# Revit family: Haworth_Enclose-Wall-Solid_Transom1
name_source: partatom
category: Furniture Systems
units: mm (PartAtom-declared; Revit-internal decimal feet)

## family parameters
Always vertical = Yes
Cut with Voids When Loaded = No
OmniClass Number = 23.25.40.14
OmniClass Title = Demountable Partitions
Part Type = Normal
Room Calculation Point = No
Round Connector Dimension = Use Diameter
Shared = Yes
Work Plane-Based = No

## types (3) — shared parameters
# of Panels Back = 1
# of Panels Front = 1
Actual # of Panels Back = 1
Actual # of Panels Front = 1
Actual Panel 1 Back Height = 32 "
Actual Panel 1 Front Height = 32 "
Actual Panel 2 Back Height = 64 "
Actual Panel 2 Front Height = 64 "
Assembly Code = C1010200
Base Height = 1.25 "
Cap Height = 1 "
Ceiling Mount = Yes
Description = Enclose Solid Wall w/ Glass Transom
End of Run Finish = Haworth - Plastic - Black
End of Run Width = 0.155 "
Frame Depth = 4 "
Frame Finish = Haworth - Brushed Aluminum
Glass Finish = Haworth - Glass - Clear
Glass Offset = 4.745 "
Glass Panel Depth = 0.4 "
Horizontal Bottom Adjuster Width = 3.87 "
Horizontal Bottom Trim Width = 2.425 "
Horizontal Frame Width = 0.875 "
Horizontal Top Adjuster Width = 2.625 "
Horizontal Top Trim Width = 1.43 "
Horizontal Transom Frame Width = 1.625 "
LEED Data = www.haworth.com/_layouts/Haworth.ProductCatalog/Handlers/GetAsset.ashx/Enclose_LEED_Contribution.pdf?cid=180&rid=1981&type=Leed
Manufacturer = Haworth
Material Options = http://surfaces.haworth.com
Max # of Panels = 3
Max. Height = 144 "
Max. Width = 60 "
Min. Height = 92 "
Min. Width = 8 "
Min/Max Height = 92-144 in.
Min/Max Width = 8-60 in.
Model = see catalog for model #
Offset Back = 1.25 "
Offset Front = 1.25 "
Panel 1 Back Height = 32 "
Panel 1 Front Height = 32 "
Panel 2 Back Height = 64 "
Panel 2 Front Height = 64 "
Panel Depth = 0.5 "
Panel Height Note = All Heights are A.F.F.
Panel Size Note = 8in increments
Raceway Panel Back = No
Raceway Panel Back Height = 8.59 "
Raceway Panel Finish = Haworth - Brushed Aluminum
Raceway Panel Front = No
Raceway Panel Front Height = 8.59 "
Revision Number = 1
Size = Verify Final Dim. w/ Haworth
Sustainability Info = www.haworth.com/en-us/About-Us/Sustainability/Documents/2005-Global-Sustainability-Report.pdf
URL = www.haworth.com
URL - Product = http://www.haworth.com
Vertical Frame Width = 0.875 "
Warranty = http://surfaces.haworth.com
zero-valued in all types: Default Elevation

## per-type parameters (varying)
| type | AFF Solid Panel Height | Actual Height | Actual Solid Panel Height | Actual Width | Height | PH1B | PH1F | Panel Height 2 | Panel Width 1 | Panel Width 2 | Raceway Panel Width | Transom Panel Height | Width |
| 36" x 108" | 88 " | 120 " | 88 " | 36 " | 120 " | 86.75 " | 86.75 " | 26.875 " | 35.69 " | 33.94 " | 35.69 " | 32 " | 36 " |
| 30" x 108" | 88 " | 108 " | 88 " | 30 " | 108 " | 86.75 " | 86.75 " | 14.875 " | 29.69 " | 27.94 " | 29.69 " | 20 " | 30 " |
| 48" x 108" | 76 " | 108 " | 76 " | 48 " | 108 " | 74.75 " | 74.75 " | 26.875 " | 47.69 " | 45.94 " | 47.69 " | 32 " | 48 " |

## geometry (parser evidence)
native form markers: Blend x4, Sweep x15
no freeform markers — native parametric forms only
